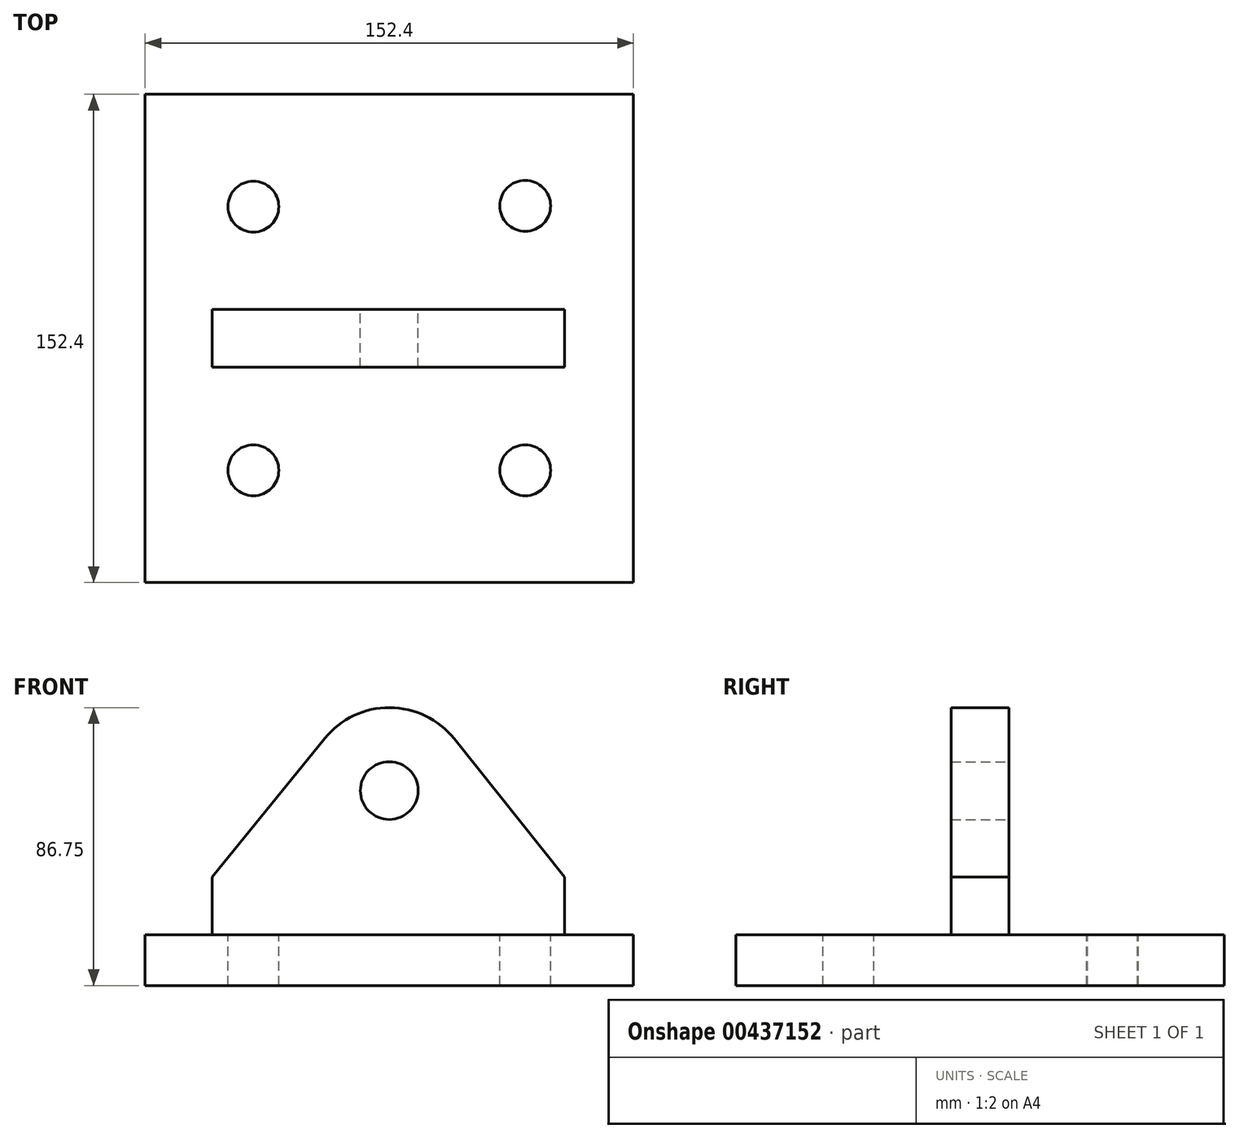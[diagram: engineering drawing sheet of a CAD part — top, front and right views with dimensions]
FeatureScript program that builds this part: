
annotation { "Feature Type Name" : "Feature", "Feature Type Description" : "" }
export const myFeature = defineFeature(function(context is Context, id is Id, definition is map)
    precondition{}
    {
        {
            var Q0;
            Q0=qCreatedBy(makeId("Front.planeOp"),FACE);
            var sketch = newSketch(context, id + "F0", { "sketchPlane" : qUnion([Q0])});
            skLineSegment(sketch, "E0", {"start": v(0, 0) * mm, "end": v(109.98, 0) * mm});
            skLineSegment(sketch, "E1", {"start": v(109.98, 0) * mm, "end": v(109.98, 18.03) * mm});
            skLineSegment(sketch, "E2", {"start": v(0, 0) * mm, "end": v(0, 18.03) * mm});
            skArc(sketch, "E3", {"start": v(75.58, 61.12) * mm, "mid": v(55.46, 70.87) * mm, "end": v(35.24, 61.32) * mm});
            skLineSegment(sketch, "E4", {"start": v(0, 18.03) * mm, "end": v(35.24, 61.32) * mm});
            skLineSegment(sketch, "E5", {"start": v(109.98, 18.03) * mm, "end": v(75.58, 61.12) * mm});
            skSolve(sketch);
        }
        {
            var Q0;
            {var subQ1=sQuery(id+"F0.wireOp",EDGE,"E1");Q0=makeQuery(id+"F0.imprint","IMPRINT",FACE,{"disambiguationData":[TD([[makeQuery(id+"F0.imprint","IMPRINT",EDGE,{"derivedFrom":subQ1}),1.0]])]});}
            extrude(context, id + "F1", {"entities" : qUnion([Q0]), "offsetDistance" : 25.4 * mm, "depth" : 18.03 * mm});
        }
        {
            var Q0;
            Q0=qCreatedBy(makeId("Top.planeOp"),FACE);
            var sketch = newSketch(context, id + "F2", { "sketchPlane" : qUnion([Q0])});
            skLineSegment(sketch, "E6.bottom", {"start": v(131.53, 67.18) * mm, "end": v(-20.87, 67.18) * mm});
            skLineSegment(sketch, "E6.top", {"start": v(131.53, -85.22) * mm, "end": v(-20.87, -85.22) * mm});
            skLineSegment(sketch, "E6.left", {"start": v(131.53, 67.18) * mm, "end": v(131.53, -85.22) * mm});
            skLineSegment(sketch, "E6.right", {"start": v(-20.87, 67.18) * mm, "end": v(-20.87, -85.22) * mm});
            skPoint(sketch, "E7", {"position": v(97.75, -50.16) * mm});
            skPoint(sketch, "E8", {"position": v(12.92, -50.16) * mm});
            skPoint(sketch, "E9", {"position": v(97.75, 32.39) * mm});
            skPoint(sketch, "E10", {"position": v(12.92, 32.13) * mm});
            skSolve(sketch);
        }
        {
            var Q0;
            Q0=makeQuery(id+"F2.imprint","IMPRINT",FACE,{"disambiguationData":[TD([[makeQuery(id+"F2.imprint","IMPRINT",EDGE,{"derivedFrom":sQuery(id+"F2.wireOp",EDGE,"E6.bottom")}),1.0]])]});
            extrude(context, id + "F3", {"entities" : qUnion([Q0]), "operationType" : NewBodyOperationType.ADD, "oppositeDirection" : true, "offsetDistance" : 25.4 * mm, "depth" : 15.88 * mm});
        }
        {
            var Q0;
            Q0=sQuery(id+"F0.wireOp",VERTEX,"E3.center");
            var Q1;
            Q1=makeQuery(id+"F1.opExtrude","SWEPT_BODY",BODY,{"disambiguationData":[OSD([sQuery(id+"F0.wireOp",EDGE,"E0"),sQuery(id+"F0.wireOp",EDGE,"E1"),sQuery(id+"F0.wireOp",EDGE,"E2"),sQuery(id+"F0.wireOp",EDGE,"E3"),sQuery(id+"F0.wireOp",EDGE,"E4"),sQuery(id+"F0.wireOp",EDGE,"E5")])]});
            hole(context, id + "F4", {"style" : HoleStyle.SIMPLE, "endStyle" : HoleEndStyle.THROUGH, "oppositeDirection" : true, "holeDiameter" : 18.03 * mm, "majorDiameter" : 6.35 * mm, "isTappedThrough" : true, "tappedDepth" : 12.7 * mm, "tapClearance" : 3, "startFromSketch" : true, "locations" : qUnion([Q0]), "scope" : qUnion([Q1])});
        }
        {
            var Q0;
            Q0=sQuery(id+"F2.wireOp",VERTEX,"E7");
            var Q1;
            Q1=sQuery(id+"F2.wireOp",VERTEX,"E8");
            var Q2;
            Q2=sQuery(id+"F2.wireOp",VERTEX,"E10");
            var Q3;
            Q3=sQuery(id+"F2.wireOp",VERTEX,"E9");
            var Q4;
            Q4=makeQuery(id+"F1.opExtrude","SWEPT_BODY",BODY,{"disambiguationData":[OSD([sQuery(id+"F0.wireOp",EDGE,"E0"),sQuery(id+"F0.wireOp",EDGE,"E1"),sQuery(id+"F0.wireOp",EDGE,"E2"),sQuery(id+"F0.wireOp",EDGE,"E3"),sQuery(id+"F0.wireOp",EDGE,"E4"),sQuery(id+"F0.wireOp",EDGE,"E5")])]});
            hole(context, id + "F5", {"style" : HoleStyle.SIMPLE, "endStyle" : HoleEndStyle.THROUGH, "holeDiameter" : 15.88 * mm, "majorDiameter" : 6.35 * mm, "isTappedThrough" : true, "tappedDepth" : 12.7 * mm, "tapClearance" : 3, "startFromSketch" : true, "locations" : qUnion([Q0, Q1, Q2, Q3]), "scope" : qUnion([Q4])});
        }
    });
